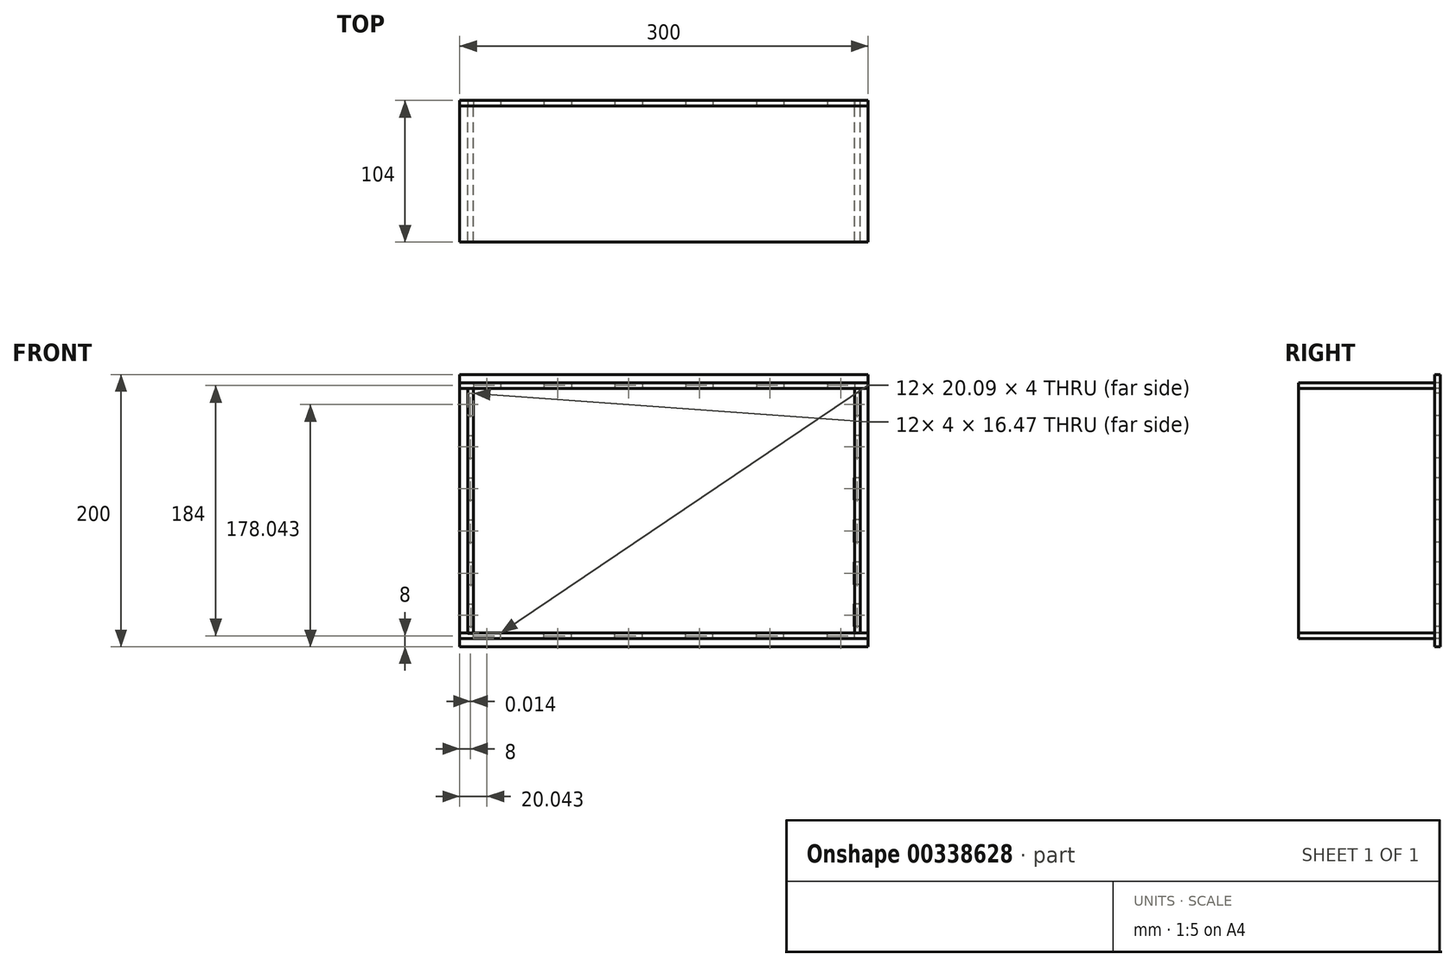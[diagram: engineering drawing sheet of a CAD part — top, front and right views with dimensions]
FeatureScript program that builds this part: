
annotation { "Feature Type Name" : "Feature", "Feature Type Description" : "" }
export const myFeature = defineFeature(function(context is Context, id is Id, definition is map)
    precondition{}
    {
        {
            assignVariable(context, id + "F0", {"name" : "Width", "anyValue" : 4});
        }
        {
            var Q0;
            Q0=qCreatedBy(makeId("Front.planeOp"),FACE);
            var sketch = newSketch(context, id + "F1", { "sketchPlane" : qUnion([Q0])});
            skLineSegment(sketch, "E0.bottom", {"start": v(-150, 100) * mm, "end": v(150, 100) * mm});
            skLineSegment(sketch, "E0.top", {"start": v(-150, -100) * mm, "end": v(150, -100) * mm});
            skLineSegment(sketch, "E0.left", {"start": v(-150, 100) * mm, "end": v(-150, -100) * mm});
            skLineSegment(sketch, "E0.right", {"start": v(150, 100) * mm, "end": v(150, -100) * mm});
            skLineSegment(sketch, "E1", {"start": v(0, -100) * mm, "end": v(0, 100) * mm, "construction": true});
            skLineSegment(sketch, "E2", {"start": v(-150, 0) * mm, "end": v(144.1, 0) * mm, "construction": true});
            skSolve(sketch);
        }
        {
            var Q0;
            Q0=makeQuery(id+"F1.imprint","IMPRINT",FACE,{"disambiguationData":[TD([[makeQuery(id+"F1.imprint","IMPRINT",EDGE,{"derivedFrom":sQuery(id+"F1.wireOp",EDGE,"E0.bottom")}),-1.0]])]});
            extrude(context, id + "F2", {"entities" : qUnion([Q0]), "depth" : (getVariable(context, 'Width')) * mm, "offsetDistance" : 25 * mm});
        }
        {
            var Q0;
            Q0=makeQuery(id+"F2.opExtrude","CAP_FACE",FACE,{"disambiguationData":[OSD([sQuery(id+"F1.wireOp",EDGE,"E0.bottom"),sQuery(id+"F1.wireOp",EDGE,"E0.top"),sQuery(id+"F1.wireOp",EDGE,"E0.left"),sQuery(id+"F1.wireOp",EDGE,"E0.right")])],"isStart":false});
            var sketch = newSketch(context, id + "F3", { "sketchPlane" : qUnion([Q0])});
            skLineSegment(sketch, "E3.0", {"start": v(-140, 90) * mm, "end": v(140, 90) * mm, "construction": true});
            skLineSegment(sketch, "E3.1", {"start": v(-140, 90) * mm, "end": v(-140, -90) * mm, "construction": true});
            skLineSegment(sketch, "E3.2", {"start": v(-140, -90) * mm, "end": v(140, -90) * mm, "construction": true});
            skLineSegment(sketch, "E3.3", {"start": v(140, 90) * mm, "end": v(140, -90) * mm, "construction": true});
            skLineSegment(sketch, "E4.bottom", {"start": v(-140, 94) * mm, "end": v(-119.91, 94) * mm});
            skLineSegment(sketch, "E4.top", {"start": v(-140, 90) * mm, "end": v(-119.91, 90) * mm});
            skLineSegment(sketch, "E4.left", {"start": v(-140, 94) * mm, "end": v(-140, 90) * mm});
            skLineSegment(sketch, "E4.right", {"start": v(-119.91, 94) * mm, "end": v(-119.91, 90) * mm});
            skLineSegment(sketch, "E5.1.0.0", {"start": v(-88, 94) * mm, "end": v(-67.91, 94) * mm});
            skLineSegment(sketch, "E5.1.0.1", {"start": v(-67.91, 94) * mm, "end": v(-67.91, 90) * mm});
            skLineSegment(sketch, "E5.1.0.2", {"start": v(-88, 90) * mm, "end": v(-67.91, 90) * mm});
            skLineSegment(sketch, "E5.1.0.3", {"start": v(-88, 94) * mm, "end": v(-88, 90) * mm});
            skLineSegment(sketch, "E5.2.0.0", {"start": v(-36, 94) * mm, "end": v(-15.91, 94) * mm});
            skLineSegment(sketch, "E5.2.0.1", {"start": v(-15.91, 94) * mm, "end": v(-15.91, 90) * mm});
            skLineSegment(sketch, "E5.2.0.2", {"start": v(-36, 90) * mm, "end": v(-15.91, 90) * mm});
            skLineSegment(sketch, "E5.2.0.3", {"start": v(-36, 94) * mm, "end": v(-36, 90) * mm});
            skLineSegment(sketch, "E5.3.0.0", {"start": v(16, 94) * mm, "end": v(36.09, 94) * mm});
            skLineSegment(sketch, "E5.3.0.1", {"start": v(36.09, 94) * mm, "end": v(36.09, 90) * mm});
            skLineSegment(sketch, "E5.3.0.2", {"start": v(16, 90) * mm, "end": v(36.09, 90) * mm});
            skLineSegment(sketch, "E5.3.0.3", {"start": v(16, 94) * mm, "end": v(16, 90) * mm});
            skLineSegment(sketch, "E5.4.0.0", {"start": v(68, 94) * mm, "end": v(88.09, 94) * mm});
            skLineSegment(sketch, "E5.4.0.1", {"start": v(88.09, 94) * mm, "end": v(88.09, 90) * mm});
            skLineSegment(sketch, "E5.4.0.2", {"start": v(68, 90) * mm, "end": v(88.09, 90) * mm});
            skLineSegment(sketch, "E5.4.0.3", {"start": v(68, 94) * mm, "end": v(68, 90) * mm});
            skLineSegment(sketch, "E5.5.0.0", {"start": v(120, 94) * mm, "end": v(140.09, 94) * mm});
            skLineSegment(sketch, "E5.5.0.1", {"start": v(140.09, 94) * mm, "end": v(140.09, 90) * mm});
            skLineSegment(sketch, "E5.5.0.2", {"start": v(120, 90) * mm, "end": v(140.09, 90) * mm});
            skLineSegment(sketch, "E5.5.0.3", {"start": v(120, 94) * mm, "end": v(120, 90) * mm});
            skLineSegment(sketch, "E5.direction1", {"start": v(-140, 94) * mm, "end": v(-88, 94) * mm, "construction": true});
            skLineSegment(sketch, "E6.bottom", {"start": v(144, 86.28) * mm, "end": v(140, 86.28) * mm});
            skLineSegment(sketch, "E6.top", {"start": v(144, 69.8) * mm, "end": v(140, 69.8) * mm});
            skLineSegment(sketch, "E6.left", {"start": v(144, 86.28) * mm, "end": v(144, 69.8) * mm});
            skLineSegment(sketch, "E6.right", {"start": v(140, 86.28) * mm, "end": v(140, 69.8) * mm});
            skLineSegment(sketch, "E7.1.0.0", {"start": v(143.99, 55.28) * mm, "end": v(143.99, 38.8) * mm});
            skLineSegment(sketch, "E7.1.0.1", {"start": v(143.99, 55.28) * mm, "end": v(139.99, 55.28) * mm});
            skLineSegment(sketch, "E7.1.0.2", {"start": v(143.99, 38.8) * mm, "end": v(139.99, 38.8) * mm});
            skLineSegment(sketch, "E7.1.0.3", {"start": v(139.99, 55.28) * mm, "end": v(139.99, 38.8) * mm});
            skLineSegment(sketch, "E7.2.0.0", {"start": v(143.97, 24.28) * mm, "end": v(143.97, 7.8) * mm});
            skLineSegment(sketch, "E7.2.0.1", {"start": v(143.97, 24.28) * mm, "end": v(139.97, 24.28) * mm});
            skLineSegment(sketch, "E7.2.0.2", {"start": v(143.97, 7.8) * mm, "end": v(139.97, 7.8) * mm});
            skLineSegment(sketch, "E7.2.0.3", {"start": v(139.97, 24.28) * mm, "end": v(139.97, 7.8) * mm});
            skLineSegment(sketch, "E7.3.0.0", {"start": v(143.96, -6.72) * mm, "end": v(143.96, -23.2) * mm});
            skLineSegment(sketch, "E7.3.0.1", {"start": v(143.96, -6.72) * mm, "end": v(139.96, -6.72) * mm});
            skLineSegment(sketch, "E7.3.0.2", {"start": v(143.96, -23.2) * mm, "end": v(139.96, -23.2) * mm});
            skLineSegment(sketch, "E7.3.0.3", {"start": v(139.96, -6.72) * mm, "end": v(139.96, -23.2) * mm});
            skLineSegment(sketch, "E7.4.0.0", {"start": v(143.94, -37.72) * mm, "end": v(143.94, -54.2) * mm});
            skLineSegment(sketch, "E7.4.0.1", {"start": v(143.94, -37.72) * mm, "end": v(139.94, -37.72) * mm});
            skLineSegment(sketch, "E7.4.0.2", {"start": v(143.94, -54.2) * mm, "end": v(139.94, -54.2) * mm});
            skLineSegment(sketch, "E7.4.0.3", {"start": v(139.94, -37.72) * mm, "end": v(139.94, -54.2) * mm});
            skLineSegment(sketch, "E7.5.0.0", {"start": v(143.93, -68.72) * mm, "end": v(143.93, -85.2) * mm});
            skLineSegment(sketch, "E7.5.0.1", {"start": v(143.93, -68.72) * mm, "end": v(139.93, -68.72) * mm});
            skLineSegment(sketch, "E7.5.0.2", {"start": v(143.93, -85.2) * mm, "end": v(139.93, -85.2) * mm});
            skLineSegment(sketch, "E7.5.0.3", {"start": v(139.93, -68.72) * mm, "end": v(139.93, -85.2) * mm});
            skLineSegment(sketch, "E7.direction1", {"start": v(144, 69.8) * mm, "end": v(143.99, 38.8) * mm, "construction": true});
            skLineSegment(sketch, "E8", {"start": v(-150, 0) * mm, "end": v(140, 0) * mm, "construction": true});
            skLineSegment(sketch, "E9", {"start": v(0, 100) * mm, "end": v(0, -90) * mm, "construction": true});
            skLineSegment(sketch, "E10.MirrorCS", {"start": v(-140, -94) * mm, "end": v(-140, -90) * mm});
            skLineSegment(sketch, "E11.MirrorCS", {"start": v(-119.91, -94) * mm, "end": v(-119.91, -90) * mm});
            skLineSegment(sketch, "E12.MirrorCS", {"start": v(-140, -94) * mm, "end": v(-119.91, -94) * mm});
            skLineSegment(sketch, "E13.MirrorCS", {"start": v(-140, -90) * mm, "end": v(-119.91, -90) * mm});
            skLineSegment(sketch, "E14.MirrorCS", {"start": v(-88, -94) * mm, "end": v(-67.91, -94) * mm});
            skLineSegment(sketch, "E15.MirrorCS", {"start": v(-67.91, -94) * mm, "end": v(-67.91, -90) * mm});
            skLineSegment(sketch, "E16.MirrorCS", {"start": v(-88, -94) * mm, "end": v(-88, -90) * mm});
            skLineSegment(sketch, "E17.MirrorCS", {"start": v(-88, -90) * mm, "end": v(-67.91, -90) * mm});
            skLineSegment(sketch, "E18.MirrorCS", {"start": v(-36, -94) * mm, "end": v(-15.91, -94) * mm});
            skLineSegment(sketch, "E19.MirrorCS", {"start": v(-15.91, -94) * mm, "end": v(-15.91, -90) * mm});
            skLineSegment(sketch, "E20.MirrorCS", {"start": v(-36, -94) * mm, "end": v(-36, -90) * mm});
            skLineSegment(sketch, "E21.MirrorCS", {"start": v(-36, -90) * mm, "end": v(-15.91, -90) * mm});
            skLineSegment(sketch, "E22.MirrorCS", {"start": v(16, -94) * mm, "end": v(16, -90) * mm});
            skLineSegment(sketch, "E23.MirrorCS", {"start": v(16, -94) * mm, "end": v(36.09, -94) * mm});
            skLineSegment(sketch, "E24.MirrorCS", {"start": v(36.09, -94) * mm, "end": v(36.09, -90) * mm});
            skLineSegment(sketch, "E25.MirrorCS", {"start": v(16, -90) * mm, "end": v(36.09, -90) * mm});
            skLineSegment(sketch, "E26.MirrorCS", {"start": v(68, -94) * mm, "end": v(88.09, -94) * mm});
            skLineSegment(sketch, "E27.MirrorCS", {"start": v(88.09, -94) * mm, "end": v(88.09, -90) * mm});
            skLineSegment(sketch, "E28.MirrorCS", {"start": v(68, -90) * mm, "end": v(88.09, -90) * mm});
            skLineSegment(sketch, "E29.MirrorCS", {"start": v(120, -94) * mm, "end": v(120, -90) * mm});
            skLineSegment(sketch, "E30.MirrorCS", {"start": v(120, -94) * mm, "end": v(140.09, -94) * mm});
            skLineSegment(sketch, "E31.MirrorCS", {"start": v(140.09, -94) * mm, "end": v(140.09, -90) * mm});
            skLineSegment(sketch, "E32.MirrorCS", {"start": v(120, -90) * mm, "end": v(140.09, -90) * mm});
            skLineSegment(sketch, "E33.MirrorCS", {"start": v(-144, 86.28) * mm, "end": v(-144, 69.8) * mm});
            skLineSegment(sketch, "E34.MirrorCS", {"start": v(-144, 86.28) * mm, "end": v(-140, 86.28) * mm});
            skLineSegment(sketch, "E35.MirrorCS", {"start": v(-144, 69.8) * mm, "end": v(-140, 69.8) * mm});
            skLineSegment(sketch, "E36.MirrorCS", {"start": v(-140, 86.28) * mm, "end": v(-140, 69.8) * mm});
            skLineSegment(sketch, "E37.MirrorCS", {"start": v(-143.99, 55.28) * mm, "end": v(-139.99, 55.28) * mm});
            skLineSegment(sketch, "E38.MirrorCS", {"start": v(-143.99, 55.28) * mm, "end": v(-143.99, 38.8) * mm});
            skLineSegment(sketch, "E39.MirrorCS", {"start": v(-143.99, 38.8) * mm, "end": v(-139.99, 38.8) * mm});
            skLineSegment(sketch, "E40.MirrorCS", {"start": v(-139.99, 55.28) * mm, "end": v(-139.99, 38.8) * mm});
            skLineSegment(sketch, "E41.MirrorCS", {"start": v(-143.97, 24.28) * mm, "end": v(-139.97, 24.28) * mm});
            skLineSegment(sketch, "E42.MirrorCS", {"start": v(-143.97, 24.28) * mm, "end": v(-143.97, 7.8) * mm});
            skLineSegment(sketch, "E43.MirrorCS", {"start": v(-143.97, 7.8) * mm, "end": v(-139.97, 7.8) * mm});
            skLineSegment(sketch, "E44.MirrorCS", {"start": v(-139.97, 24.28) * mm, "end": v(-139.97, 7.8) * mm});
            skLineSegment(sketch, "E45.MirrorCS", {"start": v(-143.96, -6.72) * mm, "end": v(-139.96, -6.72) * mm});
            skLineSegment(sketch, "E46.MirrorCS", {"start": v(-143.96, -6.72) * mm, "end": v(-143.96, -23.2) * mm});
            skLineSegment(sketch, "E47.MirrorCS", {"start": v(-143.96, -23.2) * mm, "end": v(-139.96, -23.2) * mm});
            skLineSegment(sketch, "E48.MirrorCS", {"start": v(-139.96, -6.72) * mm, "end": v(-139.96, -23.2) * mm});
            skLineSegment(sketch, "E49.MirrorCS", {"start": v(-143.94, -37.72) * mm, "end": v(-139.94, -37.72) * mm});
            skLineSegment(sketch, "E50.MirrorCS", {"start": v(-143.94, -37.72) * mm, "end": v(-143.94, -54.2) * mm});
            skLineSegment(sketch, "E51.MirrorCS", {"start": v(-143.94, -54.2) * mm, "end": v(-139.94, -54.2) * mm});
            skLineSegment(sketch, "E52.MirrorCS", {"start": v(-139.94, -37.72) * mm, "end": v(-139.94, -54.2) * mm});
            skLineSegment(sketch, "E53.MirrorCS", {"start": v(-143.93, -68.72) * mm, "end": v(-139.93, -68.72) * mm});
            skLineSegment(sketch, "E54.MirrorCS", {"start": v(-143.93, -68.72) * mm, "end": v(-143.93, -85.2) * mm});
            skLineSegment(sketch, "E55.MirrorCS", {"start": v(-143.93, -85.2) * mm, "end": v(-139.93, -85.2) * mm});
            skLineSegment(sketch, "E56.MirrorCS", {"start": v(-139.93, -68.72) * mm, "end": v(-139.93, -85.2) * mm});
            skLineSegment(sketch, "E57.MirrorCS", {"start": v(68, -94) * mm, "end": v(68, -90) * mm});
            skSolve(sketch);
        }
        {
            var Q0;
            Q0 = qSketchRegion(id + "F3", true);
            var Q1;
            Q1=makeQuery(id+"F2.opExtrude","CAP_FACE",FACE,{"disambiguationData":[OSD([sQuery(id+"F1.wireOp",EDGE,"E0.bottom"),sQuery(id+"F1.wireOp",EDGE,"E0.top"),sQuery(id+"F1.wireOp",EDGE,"E0.left"),sQuery(id+"F1.wireOp",EDGE,"E0.right")])],"isStart":true});
            extrude(context, id + "F4", {"entities" : qUnion([Q0]), "operationType" : NewBodyOperationType.REMOVE, "endBound" : BoundingType.UP_TO_SURFACE, "oppositeDirection" : true, "endBoundEntityFace" : qUnion([Q1]), "depth" : 25 * mm, "offsetDistance" : 25 * mm});
        }
        {
            var Q0;
            Q0=makeQuery(id+"F2.opExtrude","CAP_FACE",FACE,{"disambiguationData":[OSD([sQuery(id+"F1.wireOp",EDGE,"E0.bottom"),sQuery(id+"F1.wireOp",EDGE,"E0.top"),sQuery(id+"F1.wireOp",EDGE,"E0.left"),sQuery(id+"F1.wireOp",EDGE,"E0.right")])],"isStart":false});
            var sketch = newSketch(context, id + "F5", { "sketchPlane" : qUnion([Q0])});
            skLineSegment(sketch, "E58.0", {"start": v(-140, 94) * mm, "end": v(-119.91, 94) * mm});
            skLineSegment(sketch, "E58.1", {"start": v(-140, 94) * mm, "end": v(-140, 90) * mm});
            skLineSegment(sketch, "E58.2", {"start": v(-140, 90) * mm, "end": v(-119.91, 90) * mm});
            skLineSegment(sketch, "E58.3", {"start": v(-119.91, 94) * mm, "end": v(-119.91, 90) * mm});
            skLineSegment(sketch, "E58.4", {"start": v(-88, 94) * mm, "end": v(-88, 90) * mm});
            skLineSegment(sketch, "E58.5", {"start": v(-88, 90) * mm, "end": v(-67.91, 90) * mm});
            skLineSegment(sketch, "E58.6", {"start": v(-88, 94) * mm, "end": v(-67.91, 94) * mm});
            skLineSegment(sketch, "E58.7", {"start": v(-67.91, 94) * mm, "end": v(-67.91, 90) * mm});
            skLineSegment(sketch, "E58.8", {"start": v(-36, 94) * mm, "end": v(-15.91, 94) * mm});
            skLineSegment(sketch, "E58.9", {"start": v(-36, 94) * mm, "end": v(-36, 90) * mm});
            skLineSegment(sketch, "E58.10", {"start": v(-36, 90) * mm, "end": v(-15.91, 90) * mm});
            skLineSegment(sketch, "E58.11", {"start": v(-15.91, 94) * mm, "end": v(-15.91, 90) * mm});
            skLineSegment(sketch, "E58.12", {"start": v(16, 94) * mm, "end": v(36.09, 94) * mm});
            skLineSegment(sketch, "E58.13", {"start": v(16, 94) * mm, "end": v(16, 90) * mm});
            skLineSegment(sketch, "E58.14", {"start": v(16, 90) * mm, "end": v(36.09, 90) * mm});
            skLineSegment(sketch, "E58.15", {"start": v(36.09, 94) * mm, "end": v(36.09, 90) * mm});
            skLineSegment(sketch, "E58.16", {"start": v(68, 94) * mm, "end": v(68, 90) * mm});
            skLineSegment(sketch, "E58.17", {"start": v(68, 94) * mm, "end": v(88.09, 94) * mm});
            skLineSegment(sketch, "E58.18", {"start": v(68, 90) * mm, "end": v(88.09, 90) * mm});
            skLineSegment(sketch, "E58.19", {"start": v(88.09, 94) * mm, "end": v(88.09, 90) * mm});
            skLineSegment(sketch, "E58.20", {"start": v(120, 94) * mm, "end": v(120, 90) * mm});
            skLineSegment(sketch, "E58.21", {"start": v(120, 94) * mm, "end": v(140.09, 94) * mm});
            skLineSegment(sketch, "E58.22", {"start": v(120, 90) * mm, "end": v(140.09, 90) * mm});
            skLineSegment(sketch, "E58.23", {"start": v(140.09, 94) * mm, "end": v(140.09, 90) * mm});
            skSolve(sketch);
        }
        {
            var Q0;
            Q0 = qSketchRegion(id + "F5", true);
            var Q1;
            Q1=makeQuery(id+"F2.opExtrude","CAP_FACE",FACE,{"disambiguationData":[OSD([sQuery(id+"F1.wireOp",EDGE,"E0.bottom"),sQuery(id+"F1.wireOp",EDGE,"E0.top"),sQuery(id+"F1.wireOp",EDGE,"E0.left"),sQuery(id+"F1.wireOp",EDGE,"E0.right")])],"isStart":true});
            extrude(context, id + "F6", {"entities" : qUnion([Q0]), "endBound" : BoundingType.UP_TO_SURFACE, "oppositeDirection" : true, "endBoundEntityFace" : qUnion([Q1]), "depth" : 25 * mm, "offsetDistance" : 25 * mm});
        }
        {
            var Q0;
            Q0=makeQuery(id+"F2.opExtrude","CAP_FACE",FACE,{"disambiguationData":[OSD([sQuery(id+"F1.wireOp",EDGE,"E0.bottom"),sQuery(id+"F1.wireOp",EDGE,"E0.top"),sQuery(id+"F1.wireOp",EDGE,"E0.left"),sQuery(id+"F1.wireOp",EDGE,"E0.right")])],"isStart":false});
            var sketch = newSketch(context, id + "F7", { "sketchPlane" : qUnion([Q0])});
            skLineSegment(sketch, "E59.bottom", {"start": v(-150, 94) * mm, "end": v(150, 94) * mm});
            skLineSegment(sketch, "E59.top", {"start": v(-150, 90) * mm, "end": v(150, 90) * mm});
            skLineSegment(sketch, "E59.left", {"start": v(-150, 94) * mm, "end": v(-150, 90) * mm});
            skLineSegment(sketch, "E59.right", {"start": v(150, 94) * mm, "end": v(150, 90) * mm});
            skSolve(sketch);
        }
        {
            var Q0;
            Q0 = qSketchRegion(id + "F7", true);
            extrude(context, id + "F8", {"entities" : qUnion([Q0]), "depth" : 100 * mm, "offsetDistance" : 25 * mm});
        }
        {
            var Q0;
            Q0=makeQuery(id+"F2.opExtrude","CAP_FACE",FACE,{"disambiguationData":[OSD([sQuery(id+"F1.wireOp",EDGE,"E0.bottom"),sQuery(id+"F1.wireOp",EDGE,"E0.top"),sQuery(id+"F1.wireOp",EDGE,"E0.left"),sQuery(id+"F1.wireOp",EDGE,"E0.right")])],"isStart":false});
            var sketch = newSketch(context, id + "F9", { "sketchPlane" : qUnion([Q0])});
            skLineSegment(sketch, "E60.0", {"start": v(-140, -90) * mm, "end": v(-119.91, -90) * mm});
            skLineSegment(sketch, "E61.0", {"start": v(-140, -94) * mm, "end": v(-140, -90) * mm});
            skLineSegment(sketch, "E62.0", {"start": v(-140, -94) * mm, "end": v(-119.91, -94) * mm});
            skLineSegment(sketch, "E63.0", {"start": v(-119.91, -94) * mm, "end": v(-119.91, -90) * mm});
            skLineSegment(sketch, "E64.0", {"start": v(-88, -90) * mm, "end": v(-67.91, -90) * mm});
            skLineSegment(sketch, "E65.0", {"start": v(-88, -94) * mm, "end": v(-88, -90) * mm});
            skLineSegment(sketch, "E66.0", {"start": v(-88, -94) * mm, "end": v(-67.91, -94) * mm});
            skLineSegment(sketch, "E67.0", {"start": v(-67.91, -94) * mm, "end": v(-67.91, -90) * mm});
            skLineSegment(sketch, "E68.0", {"start": v(-36, -90) * mm, "end": v(-15.91, -90) * mm});
            skLineSegment(sketch, "E69.0", {"start": v(-36, -94) * mm, "end": v(-36, -90) * mm});
            skLineSegment(sketch, "E70.0", {"start": v(-36, -94) * mm, "end": v(-15.91, -94) * mm});
            skLineSegment(sketch, "E71.0", {"start": v(-15.91, -94) * mm, "end": v(-15.91, -90) * mm});
            skLineSegment(sketch, "E72.0", {"start": v(16, -94) * mm, "end": v(16, -90) * mm});
            skLineSegment(sketch, "E73.0", {"start": v(16, -90) * mm, "end": v(36.09, -90) * mm});
            skLineSegment(sketch, "E74.0", {"start": v(36.09, -94) * mm, "end": v(36.09, -90) * mm});
            skLineSegment(sketch, "E75.0", {"start": v(16, -94) * mm, "end": v(36.09, -94) * mm});
            skLineSegment(sketch, "E76.0", {"start": v(68, -94) * mm, "end": v(68, -90) * mm});
            skLineSegment(sketch, "E77.0", {"start": v(68, -90) * mm, "end": v(88.09, -90) * mm});
            skLineSegment(sketch, "E78.0", {"start": v(68, -94) * mm, "end": v(88.09, -94) * mm});
            skLineSegment(sketch, "E79.0", {"start": v(88.09, -94) * mm, "end": v(88.09, -90) * mm});
            skLineSegment(sketch, "E80.0", {"start": v(120, -90) * mm, "end": v(140.09, -90) * mm});
            skLineSegment(sketch, "E81.0", {"start": v(120, -94) * mm, "end": v(120, -90) * mm});
            skLineSegment(sketch, "E82.0", {"start": v(120, -94) * mm, "end": v(140.09, -94) * mm});
            skLineSegment(sketch, "E83.0", {"start": v(140.09, -94) * mm, "end": v(140.09, -90) * mm});
            skSolve(sketch);
        }
        {
            var Q0;
            Q0 = qSketchRegion(id + "F9", true);
            extrude(context, id + "F10", {"entities" : qUnion([Q0]), "depth" : 0.01 * mm});
        }
        {
            var Q0;
            Q0=makeQuery(id+"F2.opExtrude","CAP_FACE",FACE,{"disambiguationData":[OSD([sQuery(id+"F1.wireOp",EDGE,"E0.bottom"),sQuery(id+"F1.wireOp",EDGE,"E0.top"),sQuery(id+"F1.wireOp",EDGE,"E0.left"),sQuery(id+"F1.wireOp",EDGE,"E0.right")])],"isStart":false});
            var sketch = newSketch(context, id + "F11", { "sketchPlane" : qUnion([Q0])});
            skLineSegment(sketch, "E84.bottom", {"start": v(-150, -90) * mm, "end": v(150, -90) * mm});
            skLineSegment(sketch, "E84.top", {"start": v(-150, -94) * mm, "end": v(150, -94) * mm});
            skLineSegment(sketch, "E84.left", {"start": v(-150, -90) * mm, "end": v(-150, -94) * mm});
            skLineSegment(sketch, "E84.right", {"start": v(150, -90) * mm, "end": v(150, -94) * mm});
            skSolve(sketch);
        }
        {
            var Q0;
            Q0 = qSketchRegion(id + "F11", true);
            extrude(context, id + "F12", {"entities" : qUnion([Q0]), "depth" : 100 * mm});
        }
        {
            var Q0;
            Q0=makeQuery(id+"F2.opExtrude","CAP_FACE",FACE,{"disambiguationData":[OSD([sQuery(id+"F1.wireOp",EDGE,"E0.bottom"),sQuery(id+"F1.wireOp",EDGE,"E0.top"),sQuery(id+"F1.wireOp",EDGE,"E0.left"),sQuery(id+"F1.wireOp",EDGE,"E0.right")])],"isStart":false});
            var sketch = newSketch(context, id + "F13", { "sketchPlane" : qUnion([Q0])});
            skLineSegment(sketch, "E85.0", {"start": v(139.93, -68.72) * mm, "end": v(139.93, -85.2) * mm});
            skLineSegment(sketch, "E86.0", {"start": v(143.93, -85.2) * mm, "end": v(139.93, -85.2) * mm});
            skLineSegment(sketch, "E87.0", {"start": v(143.93, -68.72) * mm, "end": v(143.93, -85.2) * mm});
            skLineSegment(sketch, "E88.0", {"start": v(143.93, -68.72) * mm, "end": v(139.93, -68.72) * mm});
            skLineSegment(sketch, "E89.0", {"start": v(139.94, -37.72) * mm, "end": v(139.94, -54.2) * mm});
            skLineSegment(sketch, "E90.0", {"start": v(143.94, -54.2) * mm, "end": v(139.94, -54.2) * mm});
            skLineSegment(sketch, "E91.0", {"start": v(143.94, -37.72) * mm, "end": v(143.94, -54.2) * mm});
            skLineSegment(sketch, "E92.0", {"start": v(143.94, -37.72) * mm, "end": v(139.94, -37.72) * mm});
            skLineSegment(sketch, "E93.0", {"start": v(139.96, -6.72) * mm, "end": v(139.96, -23.2) * mm});
            skLineSegment(sketch, "E94.0", {"start": v(143.96, -23.2) * mm, "end": v(139.96, -23.2) * mm});
            skLineSegment(sketch, "E95.0", {"start": v(143.96, -6.72) * mm, "end": v(143.96, -23.2) * mm});
            skLineSegment(sketch, "E96.0", {"start": v(143.96, -6.72) * mm, "end": v(139.96, -6.72) * mm});
            skLineSegment(sketch, "E97.0", {"start": v(139.97, 24.28) * mm, "end": v(139.97, 7.8) * mm});
            skLineSegment(sketch, "E98.0", {"start": v(143.97, 7.8) * mm, "end": v(139.97, 7.8) * mm});
            skLineSegment(sketch, "E99.0", {"start": v(143.97, 24.28) * mm, "end": v(143.97, 7.8) * mm});
            skLineSegment(sketch, "E100.0", {"start": v(139.99, 55.28) * mm, "end": v(139.99, 38.8) * mm});
            skLineSegment(sketch, "E101.0", {"start": v(143.99, 55.28) * mm, "end": v(139.99, 55.28) * mm});
            skLineSegment(sketch, "E102.0", {"start": v(143.99, 55.28) * mm, "end": v(143.99, 38.8) * mm});
            skLineSegment(sketch, "E103.0", {"start": v(143.99, 38.8) * mm, "end": v(139.99, 38.8) * mm});
            skLineSegment(sketch, "E104.0", {"start": v(144, 86.28) * mm, "end": v(140, 86.28) * mm});
            skLineSegment(sketch, "E105.0", {"start": v(140, 86.28) * mm, "end": v(140, 69.8) * mm});
            skLineSegment(sketch, "E106.0", {"start": v(144, 69.8) * mm, "end": v(140, 69.8) * mm});
            skLineSegment(sketch, "E107.0", {"start": v(144, 86.28) * mm, "end": v(144, 69.8) * mm});
            skLineSegment(sketch, "E108.0", {"start": v(143.97, 24.28) * mm, "end": v(139.97, 24.28) * mm});
            skSolve(sketch);
        }
        {
            var Q0;
            Q0 = qSketchRegion(id + "F13", true);
            extrude(context, id + "F14", {"entities" : qUnion([Q0]), "depth" : 0.01 * mm});
        }
        {
            var Q0;
            Q0=makeQuery(id+"F13.imprint","IMPRINT",FACE,{"disambiguationData":[TD([[makeQuery(id+"F13.imprint","IMPRINT",EDGE,{"derivedFrom":sQuery(id+"F13.wireOp",EDGE,"E85.0")}),-1.0]])]});
            var sketch = newSketch(context, id + "F15", { "sketchPlane" : qUnion([Q0])});
            skLineSegment(sketch, "E109.bottom", {"start": v(140.05, -89.88) * mm, "end": v(144.33, -89.88) * mm});
            skLineSegment(sketch, "E109.top", {"start": v(140.05, 89.88) * mm, "end": v(144.33, 89.88) * mm});
            skLineSegment(sketch, "E109.left", {"start": v(140.05, -89.88) * mm, "end": v(140.05, 89.88) * mm});
            skLineSegment(sketch, "E109.right", {"start": v(144.33, -89.88) * mm, "end": v(144.33, 89.88) * mm});
            skSolve(sketch);
        }
        {
            var Q0;
            Q0 = qSketchRegion(id + "F15", true);
            extrude(context, id + "F16", {"entities" : qUnion([Q0]), "depth" : 100 * mm});
        }
        {
            var Q0;
            Q0=makeQuery(id+"F13.imprint","IMPRINT",FACE,{"disambiguationData":[TD([[makeQuery(id+"F13.imprint","IMPRINT",EDGE,{"derivedFrom":sQuery(id+"F13.wireOp",EDGE,"E85.0")}),-1.0]])]});
            var sketch = newSketch(context, id + "F17", { "sketchPlane" : qUnion([Q0])});
            skLineSegment(sketch, "E110.0", {"start": v(-144, 86.28) * mm, "end": v(-140, 86.28) * mm});
            skLineSegment(sketch, "E111.0", {"start": v(-140, 86.28) * mm, "end": v(-140, 69.8) * mm});
            skLineSegment(sketch, "E112.0", {"start": v(-144, 86.28) * mm, "end": v(-144, 69.8) * mm});
            skLineSegment(sketch, "E113.0", {"start": v(-144, 69.8) * mm, "end": v(-140, 69.8) * mm});
            skLineSegment(sketch, "E114.0", {"start": v(-139.99, 55.28) * mm, "end": v(-139.99, 38.8) * mm});
            skLineSegment(sketch, "E115.0", {"start": v(-143.99, 38.8) * mm, "end": v(-139.99, 38.8) * mm});
            skLineSegment(sketch, "E116.0", {"start": v(-143.99, 55.28) * mm, "end": v(-143.99, 38.8) * mm});
            skLineSegment(sketch, "E117.0", {"start": v(-143.99, 55.28) * mm, "end": v(-139.99, 55.28) * mm});
            skLineSegment(sketch, "E118.0", {"start": v(-139.97, 24.28) * mm, "end": v(-139.97, 7.8) * mm});
            skLineSegment(sketch, "E119.0", {"start": v(-143.97, 24.28) * mm, "end": v(-139.97, 24.28) * mm});
            skLineSegment(sketch, "E120.0", {"start": v(-143.97, 24.28) * mm, "end": v(-143.97, 7.8) * mm});
            skLineSegment(sketch, "E121.0", {"start": v(-143.97, 7.8) * mm, "end": v(-139.97, 7.8) * mm});
            skLineSegment(sketch, "E122.0", {"start": v(-139.96, -6.72) * mm, "end": v(-139.96, -23.2) * mm});
            skLineSegment(sketch, "E123.0", {"start": v(-143.96, -6.72) * mm, "end": v(-139.96, -6.72) * mm});
            skLineSegment(sketch, "E124.0", {"start": v(-143.96, -6.72) * mm, "end": v(-143.96, -23.2) * mm});
            skLineSegment(sketch, "E125.0", {"start": v(-143.96, -23.2) * mm, "end": v(-139.96, -23.2) * mm});
            skLineSegment(sketch, "E126.0", {"start": v(-139.94, -37.72) * mm, "end": v(-139.94, -54.2) * mm});
            skLineSegment(sketch, "E127.0", {"start": v(-143.94, -37.72) * mm, "end": v(-139.94, -37.72) * mm});
            skLineSegment(sketch, "E128.0", {"start": v(-143.94, -54.2) * mm, "end": v(-139.94, -54.2) * mm});
            skLineSegment(sketch, "E129.0", {"start": v(-143.94, -37.72) * mm, "end": v(-143.94, -54.2) * mm});
            skLineSegment(sketch, "E130.0", {"start": v(-139.93, -68.72) * mm, "end": v(-139.93, -85.2) * mm});
            skLineSegment(sketch, "E131.0", {"start": v(-143.93, -68.72) * mm, "end": v(-139.93, -68.72) * mm});
            skLineSegment(sketch, "E132.0", {"start": v(-143.93, -85.2) * mm, "end": v(-139.93, -85.2) * mm});
            skLineSegment(sketch, "E133.0", {"start": v(-143.93, -68.72) * mm, "end": v(-143.93, -85.2) * mm});
            skSolve(sketch);
        }
        {
            var Q0;
            Q0 = qSketchRegion(id + "F17", true);
            extrude(context, id + "F18", {"entities" : qUnion([Q0]), "depth" : 0.01 * mm});
        }
        {
            var Q0;
            Q0=makeQuery(id+"F13.imprint","IMPRINT",FACE,{"disambiguationData":[TD([[makeQuery(id+"F13.imprint","IMPRINT",EDGE,{"derivedFrom":sQuery(id+"F13.wireOp",EDGE,"E85.0")}),-1.0]])]});
            var sketch = newSketch(context, id + "F19", { "sketchPlane" : qUnion([Q0])});
            skLineSegment(sketch, "E134.bottom", {"start": v(-139.96, 90) * mm, "end": v(-144.06, 90) * mm});
            skLineSegment(sketch, "E134.top", {"start": v(-139.96, -90.06) * mm, "end": v(-144.06, -90.06) * mm});
            skLineSegment(sketch, "E134.left", {"start": v(-139.96, 90) * mm, "end": v(-139.96, -90.06) * mm});
            skLineSegment(sketch, "E134.right", {"start": v(-144.06, 90) * mm, "end": v(-144.06, -90.06) * mm});
            skSolve(sketch);
        }
        {
            var Q0;
            Q0 = qSketchRegion(id + "F19", true);
            extrude(context, id + "F20", {"entities" : qUnion([Q0]), "depth" : 100 * mm});
        }
    });
